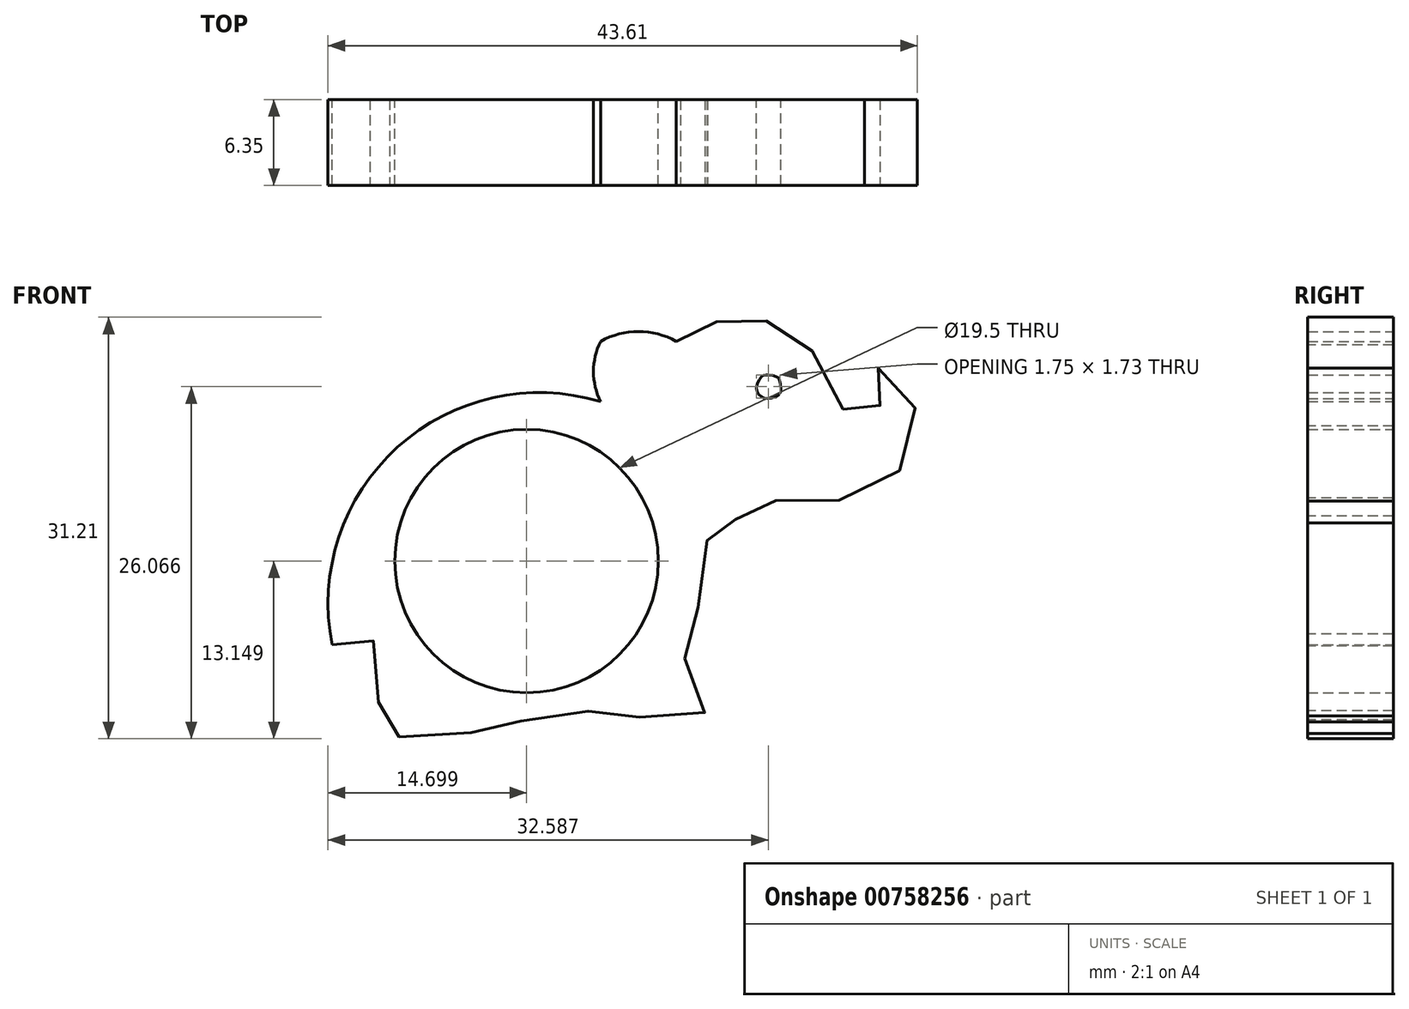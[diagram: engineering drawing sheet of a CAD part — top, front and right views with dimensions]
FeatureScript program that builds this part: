
annotation { "Feature Type Name" : "Feature", "Feature Type Description" : "" }
export const myFeature = defineFeature(function(context is Context, id is Id, definition is map)
    precondition{}
    {
        {
            var Q0;
            Q0=qCreatedBy(makeId("Front.planeOp"),FACE);
            var sketch = newSketch(context, id + "F0", { "sketchPlane" : qUnion([Q0])});
            skCircle(sketch, "E0", {"center": v(-8.64, -8.13) * mm, "radius": 9.75 * mm});
            skArc(sketch, "E1", {"start": v(-3.17, 3.68) * mm, "mid": v(-18.2, 0.3) * mm, "end": v(-23.04, -14.32) * mm});
            skArc(sketch, "E2", {"start": v(-3.17, 8.14) * mm, "mid": v(-3.69, 5.9) * mm, "end": v(-3.17, 3.68) * mm});
            skArc(sketch, "E3", {"start": v(2.45, 8.14) * mm, "mid": v(-0.36, 8.87) * mm, "end": v(-3.17, 8.14) * mm});
            skFitSpline(sketch, "E4", {"points": [v(2.45, 8.14) * mm, v(2.78, 7.87) * mm, v(3.08, 8.41) * mm, v(3.75, 8.9) * mm, v(4.63, 9.32) * mm, v(5.54, 9.63) * mm, v(6.36, 9.84) * mm, v(7.12, 9.93) * mm, v(7.9, 9.87) * mm, v(8.66, 9.75) * mm, v(9.57, 9.5) * mm, v(10.51, 9.18) * mm, v(11.46, 8.5) * mm, v(12.03, 8.14) * mm, v(12.67, 7.15) * mm, v(13.19, 6.15) * mm, v(13.85, 4.75) * mm, v(14.58, 3.57) * mm, v(15.28, 2.3) * mm, v(16.31, 1.87) * mm, v(17.07, 2.24) * mm, v(17.43, 2.81) * mm, v(17.43, 3.75) * mm, v(16.8, 4.36) * mm, v(16.37, 4.9) * mm, v(16.58, 5.66) * mm, v(17.13, 6.12) * mm, v(18.04, 6.03) * mm, v(19.04, 5.3) * mm, v(19.59, 4.7) * mm, v(19.98, 3.7) * mm, v(20.25, 2.51) * mm, v(20.16, 1.12) * mm, v(19.71, -0.13) * mm, v(18.95, -1.46) * mm, v(17.59, -2.62) * mm, v(16.13, -3.28) * mm, v(15.01, -3.56) * mm, v(13.68, -3.68) * mm, v(11.61, -3.62) * mm, v(10.67, -3.5) * mm, v(9.95, -3.52) * mm, v(9.62, -4.06) * mm, v(9.53, -4.74) * mm, v(9.03, -5.25) * mm, v(7.92, -5.22) * mm, v(6.49, -5.02) * mm, v(5.71, -4.87) * mm, v(4.94, -4.87) * mm, v(4.58, -5.35) * mm, v(4.67, -6.06) * mm, v(4.73, -7.46) * mm, v(4.61, -9.1) * mm, v(4.37, -10.57) * mm, v(4.02, -11.64) * mm, v(3.42, -12.69) * mm, v(3, -13.61) * mm, v(2.76, -14.21) * mm, v(2.94, -15.2) * mm, v(3.66, -15.91) * mm, v(4.29, -17.22) * mm, v(4.65, -18.69) * mm, v(4.65, -19.25) * mm, v(3.66, -19.55) * mm, v(2.45, -19.58) * mm, v(1.27, -19.61) * mm, v(-0.49, -19.7) * mm, v(-2.07, -19.92) * mm, v(-3.02, -20) * mm, v(-3.6, -19.62) * mm, v(-3.86, -19.32) * mm, v(-4.79, -19.23) * mm, v(-6.34, -19.65) * mm, v(-7.6, -19.89) * mm, v(-9.26, -19.98) * mm, v(-10.4, -19.9) * mm, v(-11.38, -19.92) * mm, v(-12, -20.22) * mm, v(-12.52, -20.76) * mm, v(-13.68, -20.88) * mm, v(-15.32, -20.97) * mm, v(-17, -21.06) * mm, v(-18.75, -21.2) * mm, v(-19.74, -21.21) * mm, v(-20.22, -20.55) * mm, v(-19.95, -19.42) * mm, v(-19.23, -17.69) * mm, v(-18.79, -16.25) * mm, v(-19.3, -14.97) * mm, v(-19.98, -14.05) * mm, v(-20.31, -13.54) * mm, v(-20.94, -13.66) * mm, v(-21.53, -13.99) * mm, v(-22.2, -14.38) * mm, v(-23.04, -14.32) * mm], "startDerivative": vector(54.06, -66.42) * mm, "endDerivative": vector(-92.33, 19.36) * mm});
            skFitSpline(sketch, "E5", {"points": [v(8.58, 5.31) * mm, v(8.88, 5.61) * mm, v(9.31, 5.64) * mm, v(9.95, 5.48) * mm, v(10.11, 5.11) * mm, v(10.15, 4.36) * mm, v(9.51, 3.95) * mm, v(8.85, 3.98) * mm, v(8.45, 4.36) * mm, v(8.38, 4.75) * mm, v(8.58, 5.31) * mm]});
            skSolve(sketch);
        }
        {
            var Q0;
            Q0=makeQuery(id+"F0.imprint","IMPRINT",FACE,{"disambiguationData":[TD([[makeQuery(id+"F0.imprint","IMPRINT",EDGE,{"derivedFrom":sQuery(id+"F0.wireOp",EDGE,"E0")}),-1.0]])]});
            extrude(context, id + "F1", {"entities" : qUnion([Q0]), "depth" : 6.35 * mm, "offsetDistance" : 25.4 * mm});
        }
    });
